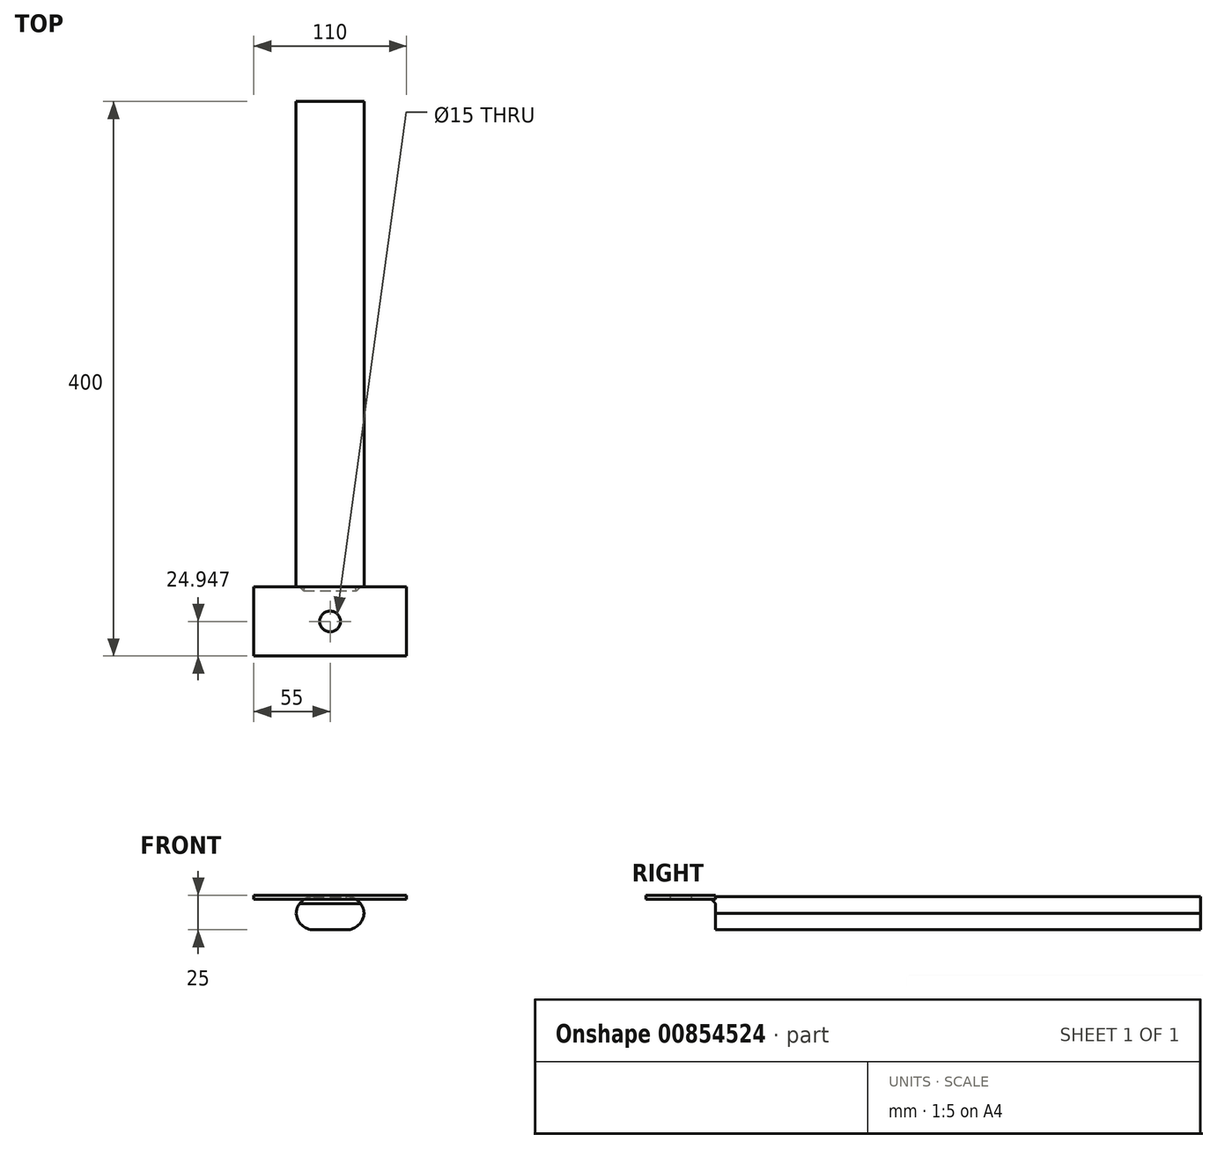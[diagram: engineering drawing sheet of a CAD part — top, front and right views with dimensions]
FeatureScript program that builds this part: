
annotation { "Feature Type Name" : "Feature", "Feature Type Description" : "" }
export const myFeature = defineFeature(function(context is Context, id is Id, definition is map)
    precondition{}
    {
        {
            var Q0;
            Q0=qCreatedBy(makeId("Front.planeOp"),FACE);
            var sketch = newSketch(context, id + "F0", { "sketchPlane" : qUnion([Q0])});
            skLineSegment(sketch, "E0.bottom", {"start": v(12.7, 0) * mm, "end": v(36.3, 0) * mm});
            skLineSegment(sketch, "E0.top", {"start": v(12.7, 24) * mm, "end": v(36.3, 24) * mm});
            skLineSegment(sketch, "E0.left", {"start": v(0, 11.3) * mm, "end": v(0, 12.7) * mm});
            skLineSegment(sketch, "E0.right", {"start": v(49, 11.3) * mm, "end": v(49, 12.7) * mm});
            skPoint(sketch, "E1.visualSharp", {"position": v(0, 24) * mm});
            skArc(sketch, "E1.filletArc", {"start": v(12.7, 24) * mm, "mid": v(3.72, 20.28) * mm, "end": v(0, 11.3) * mm});
            skPoint(sketch, "E2.visualSharp", {"position": v(0, 0) * mm});
            skArc(sketch, "E2.filletArc", {"start": v(0, 12.7) * mm, "mid": v(3.72, 3.72) * mm, "end": v(12.7, 0) * mm});
            skPoint(sketch, "E3.visualSharp", {"position": v(49, 0) * mm});
            skArc(sketch, "E3.filletArc", {"start": v(36.3, 0) * mm, "mid": v(45.28, 3.72) * mm, "end": v(49, 12.7) * mm});
            skPoint(sketch, "E4.visualSharp", {"position": v(49, 24) * mm});
            skArc(sketch, "E4.filletArc", {"start": v(49, 11.3) * mm, "mid": v(45.28, 20.28) * mm, "end": v(36.3, 24) * mm});
            skSolve(sketch);
        }
        {
            var Q0;
            {var subQ1=sQuery(id+"F0.wireOp",EDGE,"E0.bottom");Q0=makeQuery(id+"F0.imprint","IMPRINT",FACE,{"disambiguationData":[TD([[makeQuery(id+"F0.imprint","IMPRINT",EDGE,{"derivedFrom":subQ1}),1.0]])]});}
            extrude(context, id + "F1", {"entities" : qUnion([Q0]), "endBound" : BoundingType.SYMMETRIC, "depth" : 350 * mm, "offsetDistance" : 25.4 * mm});
        }
        {
            var Q0;
            Q0=makeQuery(id+"F1.opExtrude","SWEPT_FACE",FACE,{"disambiguationData":[OSD([sQuery(id+"F0.wireOp",EDGE,"E0.bottom")])]});
            var sketch = newSketch(context, id + "F2", { "sketchPlane" : qUnion([Q0])});
            skLineSegment(sketch, "E5", {"start": v(79.5, 200) * mm, "end": v(79.5, 225) * mm});
            skLineSegment(sketch, "E6", {"start": v(79.5, 225) * mm, "end": v(-30.5, 225) * mm});
            skLineSegment(sketch, "E7", {"start": v(-30.5, 225) * mm, "end": v(-30.5, 175) * mm});
            skLineSegment(sketch, "E8", {"start": v(-30.5, 175) * mm, "end": v(79.5, 175) * mm});
            skLineSegment(sketch, "E9", {"start": v(79.5, 200) * mm, "end": v(79.5, 175) * mm});
            skSolve(sketch);
        }
        {
            var Q0;
            Q0 = qSketchRegion(id + "F2", true);
            extrude(context, id + "F3", {"entities" : qUnion([Q0]), "operationType" : NewBodyOperationType.ADD, "oppositeDirection" : true, "depth" : 25 * mm, "offsetDistance" : 25 * mm});
        }
        {
            var Q0;
            Q0=makeQuery(id+"F3.boolean.opBoolean","MERGE",FACE,{"derivedFrom":[makeQuery(id+"F1.opExtrude","SWEPT_FACE",FACE,{"disambiguationData":[OSD([sQuery(id+"F0.wireOp",EDGE,"E0.bottom")])]}),makeQuery(id+"F3.opExtrude","CAP_FACE",FACE,{"disambiguationData":[OSD([sQuery(id+"F2.wireOp",EDGE,"E5"),sQuery(id+"F2.wireOp",EDGE,"E6"),sQuery(id+"F2.wireOp",EDGE,"E7"),sQuery(id+"F2.wireOp",EDGE,"E8"),sQuery(id+"F2.wireOp",EDGE,"E9")])],"isStart":true})]});
            var sketch = newSketch(context, id + "F4", { "sketchPlane" : qUnion([Q0])});
            skLineSegment(sketch, "E10.bottom", {"start": v(-30.5, 225) * mm, "end": v(79.5, 225) * mm});
            skLineSegment(sketch, "E10.top", {"start": v(-30.5, 175) * mm, "end": v(79.5, 175) * mm});
            skLineSegment(sketch, "E10.left", {"start": v(-30.5, 225) * mm, "end": v(-30.5, 175) * mm});
            skLineSegment(sketch, "E10.right", {"start": v(79.5, 225) * mm, "end": v(79.5, 175) * mm});
            skSolve(sketch);
        }
        {
            var Q0;
            Q0 = qSketchRegion(id + "F4", true);
            extrude(context, id + "F5", {"entities" : qUnion([Q0]), "operationType" : NewBodyOperationType.REMOVE, "oppositeDirection" : true, "depth" : 22 * mm, "offsetDistance" : 25 * mm});
        }
        {
            var Q0;
            {var subQ0=sQuery(id+"F4.wireOp",EDGE,"E10.top");Q0=makeQuery(id+"F5.boolean.opBoolean","COPY",EDGE,{"disambiguationData":[topologyDisambiguationEdgeConnected([makeQuery(id+"F5.opExtrude","CAP_FACE",FACE,{"disambiguationData":[OSD([sQuery(id+"F4.wireOp",EDGE,"E10.bottom"),subQ0,sQuery(id+"F4.wireOp",EDGE,"E10.left"),sQuery(id+"F4.wireOp",EDGE,"E10.right")])],"isStart":false}),makeQuery(id+"F5.opExtrude","SWEPT_FACE",FACE,{"disambiguationData":[OSD([subQ0])]})])],"derivedFrom":makeQuery(id+"F5.opExtrude","CAP_EDGE",EDGE,{"disambiguationData":[OSD([subQ0])],"isStart":false})});}
            chamfer(context, id + "F6", {"entities" : qUnion([Q0]), "width" : 3 * mm, "tangentPropagation" : true});
        }
        {
            var Q0;
            Q0=makeQuery(id+"F5.boolean.opBoolean","COPY",FACE,{"derivedFrom":makeQuery(id+"F5.opExtrude","CAP_FACE",FACE,{"disambiguationData":[OSD([sQuery(id+"F4.wireOp",EDGE,"E10.bottom"),sQuery(id+"F4.wireOp",EDGE,"E10.top"),sQuery(id+"F4.wireOp",EDGE,"E10.left"),sQuery(id+"F4.wireOp",EDGE,"E10.right")])],"isStart":false})});
            var sketch = newSketch(context, id + "F7", { "sketchPlane" : qUnion([Q0])});
            skCircle(sketch, "E11", {"center": v(24.5, 200.05) * mm, "radius": 7.5 * mm});
            skSolve(sketch);
        }
        {
            var Q0;
            Q0 = qSketchRegion(id + "F7", true);
            extrude(context, id + "F8", {"entities" : qUnion([Q0]), "operationType" : NewBodyOperationType.REMOVE, "oppositeDirection" : true, "depth" : 25 * mm, "offsetDistance" : 25 * mm});
        }
    });
